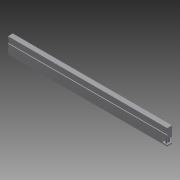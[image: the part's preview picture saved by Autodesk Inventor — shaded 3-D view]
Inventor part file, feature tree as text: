
AUTODESK INVENTOR PART (.ipt)
format: ipt  version: 2012 (Build 160160000, 160)  size: 94,208 bytes
history: native  units: in
note: dims shown in document units (in); Inventor stores cm internally (conversion verified against a paired STEP export)
features: extrude x4, sketch x4
ambient origin geometry x8: Origin, YZ Plane, XZ Plane, XY Plane, X Axis, Y Axis, Z Axis, Center Point
bodies: Solid1 (feature_tree)
feature tree (8):
  extrude  "Extrusion1"  Depth=1.0in
  extrude  "Extrusion2"  Depth=10.0in
  extrude  "Extrusion3"  Depth=0.05in TaperAngle=0.0deg
  extrude  "Extrusion4"  Depth=0.3in
  sketch  "Sketch1"  dims[d0=10.0in d1=1.0in]
  sketch  "Sketch2"  dims[d2=0.3in d3=0.0in d4=10.0in]
  sketch  "Sketch3"  dims[d5=0.25in d6=0.05in d7=0.0in]
  sketch  "Sketch4"  dims[d8=0.3in d9=0.3in d10=0.3in d11=0.0in d14=0.3in d15=0.0in]
